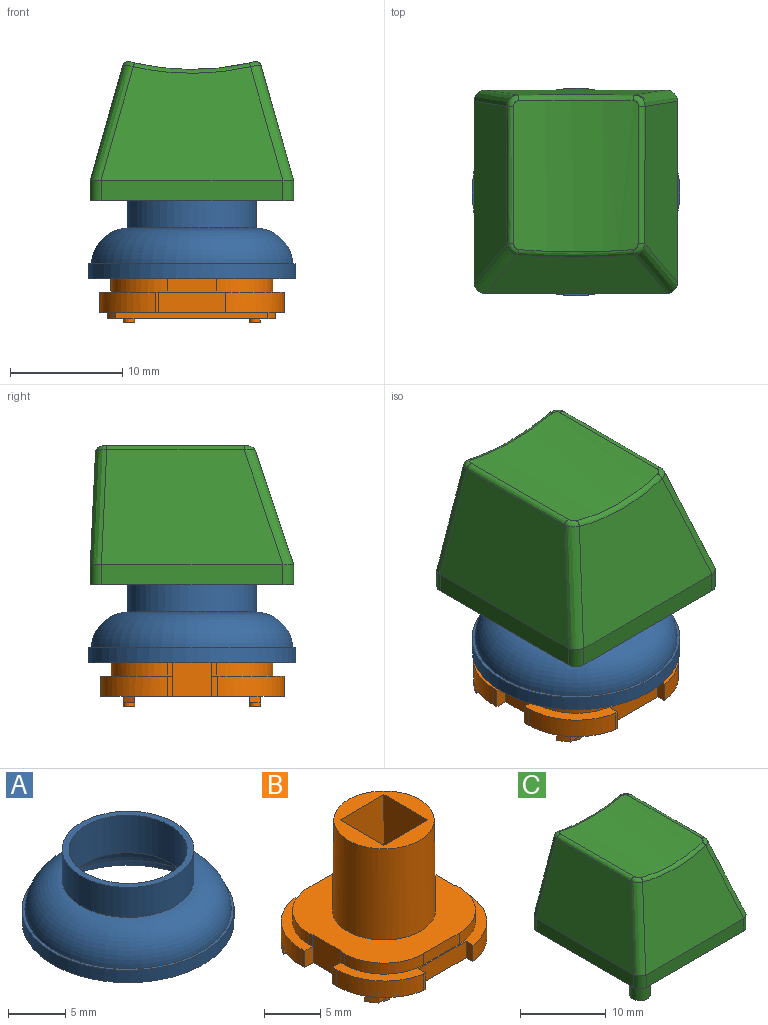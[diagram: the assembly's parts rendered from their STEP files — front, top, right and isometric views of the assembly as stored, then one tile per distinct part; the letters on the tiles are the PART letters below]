
ASSEMBLY  parts=3 mates=2
PART A: 9 faces, bbox 19.5x19.5x7.7 mm
  f0: cylinder r=9.25mm len=18.5mm, axis (0,0,1), area 76.2mm2, adj f1,f8
  f1: plane 18.5x18.5mm, normal (0,0,-1), area 41.8mm2, adj f0,f2
  f2: cylinder r=8.5mm len=17mm, axis (0,0,1), area 27.5mm2, adj f1,f3
  f3: torus R=5.16mm, axis (0,0,1), area 232.3mm2, adj f2,f4
  f4: cylinder r=5.15mm len=10.3mm, axis (0,0,1), area 129.4mm2, adj f3,f5
  f5: plane 11.5x11.5mm, normal (0,0,1), area 20.5mm2, adj f4,f6
  f6: cylinder r=5.75mm len=11.5mm, axis (0,0,1), area 115.6mm2, adj f5,f7
  f7: torus R=5.6mm, axis (0,0,1), area 243.6mm2, adj f6,f8
  f8: plane 18.5x18.5mm, normal (0,0,1), area 14.3mm2, adj f0,f7
PART B: 86 faces, bbox 16.4x16.4x13.7 mm
  f0: plane 6x1.8mm, normal (0,1,0), area 10.8mm2, adj f3,f10,f11,f12
  f1: plane 1x1mm, normal (0,0,-1), area 0.8mm2, adj f13
  f2: plane 1x1mm, normal (0,0,-1), area 0.8mm2, adj f14
  f3: plane 1.8x0.85mm, normal (1,0,0), area 1.5mm2, adj f0,f11,f12,f26
  f4: plane 1.2x0.45mm, normal (-1,0,0), area 0.5mm2, adj f5,f11,f27,f28
  f5: revolved ~5x5mm, area 9.4mm2, adj f4,f6,f11,f28
  f6: plane 4.4x1.2mm, normal (0,1,0), area 5.3mm2, adj f5,f7,f11,f28
  f7: revolved ~5x5mm, area 9.4mm2, adj f6,f9,f11,f28
  f8: revolved ~9.8x9.13mm, area 277.6mm2, adj f19,f28
  f9: plane 1.2x0.45mm, normal (1,0,0), area 0.5mm2, adj f7,f11,f28,f29
  f10: plane 1.8x0.85mm, normal (-1,0,0), area 1.5mm2, adj f0,f11,f12,f31
  f11: plane 16.4x6.4mm, normal (0,0,1), area 17.2mm2, adj f0,f3,f4,f5,f6,f7,f9,f10
  f12: plane 13.52x2.05mm, normal (0,0,-1), area 17.2mm2, adj f0,f3,f10,f15,f26,f31
  f13: revolved ~1x1mm, area 0.9mm2, adj f1,f32,f33
  f14: revolved ~1x1mm, area 0.9mm2, adj f2,f33,f34
  f15: plane 13.52x0.6mm, normal (0,1,0), area 8.1mm2, adj f12,f32,f33,f34,f35,f36
  f16: plane 2.8x0.75mm, normal (0,0,-1), area 2.1mm2, adj f40,f41,f42,f43
  f17: plane 2.8x0.75mm, normal (0,0,-1), area 2.1mm2, adj f44,f45,f46,f47
  f18: plane 2.8x0.75mm, normal (0,0,-1), area 2.1mm2, adj f48,f49,f50,f51
  f19: plane 8.9x8.9mm, normal (0,0,1), area 32mm2, adj f8,f43,f47,f51,f52
  f20: plane 2.8x0.75mm, normal (0,0,-1), area 2.1mm2, adj f37,f38,f39,f52
  f21: revolved ~5x5mm, area 9.4mm2, adj f22,f24,f28,f55
  f22: plane 4.4x1.2mm, normal (0,-1,0), area 5.3mm2, adj f21,f23,f28,f55
  f23: revolved ~5x5mm, area 9.4mm2, adj f22,f28,f53,f55
  f24: plane 1.2x0.45mm, normal (1,0,0), area 0.5mm2, adj f21,f28,f55,f57
  f25: plane 1.8x0.45mm, normal (-1,0,0), area 0.8mm2, adj f11,f26,f27,f58
  f26: revolved ~5.95x5.2mm, area 15.5mm2, adj f3,f11,f12,f25,f35,f58
  f27: plane 3x1.1mm, normal (0,-1,0), area 2.1mm2, adj f4,f11,f25,f28,f58,f59,f72
  f28: plane 14.4x14.4mm, normal (0,0,1), area 119.7mm2, adj f4,f5,f6,f7,f8,f9,f21,f22
  f29: plane 3x1.1mm, normal (0,-1,0), area 2.1mm2, adj f9,f11,f28,f30,f60,f61,f72
  f30: plane 1.8x0.45mm, normal (1,0,0), area 0.8mm2, adj f11,f29,f31,f61
  f31: revolved ~5.95x5.2mm, area 15.5mm2, adj f10,f11,f12,f30,f36,f61
  f32: plane 1.86x1mm, normal (0,0,-1), area 1.1mm2, adj f13,f15,f36,f62
  f33: plane 11.2x1mm, normal (0,0,-1), area 10.4mm2, adj f13,f14,f15,f62
  f34: plane 1.85x1mm, normal (0,0,-1), area 1.1mm2, adj f14,f15,f35,f62
  f35: revolved ~1x0.69mm, area 0.7mm2, adj f15,f26,f34,f62
  f36: revolved ~1x0.69mm, area 0.7mm2, adj f15,f31,f32,f62
  f37: plane 5.9x0.75mm, normal (0,1,0), area 4.4mm2, adj f20,f38,f52,f63
  f38: plane 5.9x2.8mm, normal (1,0,0), area 16.5mm2, adj f20,f37,f39,f63
  f39: plane 5.9x0.75mm, normal (0,-1,0), area 4.4mm2, adj f20,f38,f52,f63
  f40: plane 5.9x0.75mm, normal (1,0,0), area 4.4mm2, adj f16,f41,f43,f63
  f41: plane 5.9x2.8mm, normal (0,-1,0), area 16.5mm2, adj f16,f40,f42,f63
  f42: plane 5.9x0.75mm, normal (-1,0,0), area 4.4mm2, adj f16,f41,f43,f63
  f43: plane 12.8x5.5mm, normal (0,-1,0), area 53.9mm2, adj f16,f19,f40,f42,f47,f52,f63
  f44: plane 5.9x0.75mm, normal (0,-1,0), area 4.4mm2, adj f17,f45,f47,f63
  f45: plane 5.9x2.8mm, normal (-1,0,0), area 16.5mm2, adj f17,f44,f46,f63
  f46: plane 5.9x0.75mm, normal (0,1,0), area 4.4mm2, adj f17,f45,f47,f63
  f47: plane 12.8x5.5mm, normal (-1,0,0), area 53.9mm2, adj f17,f19,f43,f44,f46,f51,f63
  f48: plane 5.9x0.75mm, normal (-1,0,0), area 4.4mm2, adj f18,f49,f51,f63
  f49: plane 5.9x2.8mm, normal (0,1,0), area 16.5mm2, adj f18,f48,f50,f63
  f50: plane 5.9x0.75mm, normal (1,0,0), area 4.4mm2, adj f18,f49,f51,f63
  f51: plane 12.8x5.5mm, normal (0,1,0), area 53.9mm2, adj f18,f19,f47,f48,f50,f52,f63
  f52: plane 12.8x5.5mm, normal (1,0,0), area 53.9mm2, adj f19,f20,f37,f39,f43,f51,f63
  f53: plane 1.2x0.45mm, normal (-1,0,0), area 0.5mm2, adj f23,f28,f55,f64
  f54: plane 1.8x0.2mm, normal (0,-1,0), area 0.4mm2, adj f55,f66,f70,f77
  f55: plane 16.4x6.45mm, normal (0,0,1), area 17.6mm2, adj f21,f22,f23,f24,f53,f54,f56,f57
  f56: plane 1.8x0.45mm, normal (1,0,0), area 0.8mm2, adj f55,f57,f69,f71
  f57: plane 3x1.1mm, normal (0,1,0), area 2.1mm2, adj f24,f28,f55,f56,f60,f71,f72
  f58: plane 3.35x1.93mm, normal (0,0,-1), area 3.5mm2, adj f25,f26,f27,f62,f72
  f59: plane 3.5x3mm, normal (-1,0,0), area 10.5mm2, adj f27,f28,f64,f72
  f60: plane 3.5x3mm, normal (1,0,0), area 10.5mm2, adj f28,f29,f57,f72
  f61: plane 3.35x1.93mm, normal (0,0,-1), area 3.5mm2, adj f29,f30,f31,f62,f72
  f62: plane 14.91x0.6mm, normal (0,-1,0), area 8.9mm2, adj f32,f33,f34,f35,f36,f58,f61,f72
  f63: plane 9.2x9.2mm, normal (0,0,-1), area 27.8mm2, adj f37,f38,f39,f40,f41,f42,f43,f44
  f64: plane 3x1.1mm, normal (0,1,0), area 2.1mm2, adj f28,f53,f55,f59,f65,f72,f73
  f65: plane 1.8x0.53mm, normal (-1,0,0), area 1mm2, adj f55,f64,f70,f73
  f66: plane 1.8x0.9mm, normal (1,0,0), area 1.6mm2, adj f54,f55,f67,f77
  f67: plane 6x1.8mm, normal (0,-1,0), area 10.8mm2, adj f55,f66,f68,f77
  f68: plane 1.8x0.85mm, normal (-1,0,0), area 1.5mm2, adj f55,f67,f69,f77
  f69: revolved ~5.95x5.2mm, area 15.5mm2, adj f55,f56,f68,f71,f75,f77
  f70: revolved ~5.92x5mm, area 15.2mm2, adj f54,f55,f65,f73,f77,f78
  f71: plane 3.35x1.93mm, normal (0,0,-1), area 3.5mm2, adj f56,f57,f69,f72,f79
  f72: plane 14.4x10.2mm, normal (0,0,-1), area 76.3mm2, adj f27,f29,f57,f58,f59,f60,f61,f62
  f73: plane 3.35x1.93mm, normal (0,0,-1), area 3.6mm2, adj f64,f65,f70,f72,f79
  f74: plane 1x1mm, normal (0,0,-1), area 0.8mm2, adj f80
  f75: revolved ~1x0.69mm, area 0.7mm2, adj f69,f76,f79,f81
  f76: plane 1.86x1mm, normal (0,0,-1), area 1.1mm2, adj f75,f79,f80,f81
  f77: plane 13.59x2.1mm, normal (0,0,-1), area 17.5mm2, adj f54,f66,f67,f68,f69,f70,f81
  f78: revolved ~1x0.67mm, area 0.7mm2, adj f70,f79,f81,f82
  f79: plane 14.95x0.6mm, normal (0,1,0), area 9mm2, adj f71,f72,f73,f75,f76,f78,f82,f83
  f80: revolved ~1x1mm, area 0.9mm2, adj f74,f76,f83
  f81: plane 13.59x0.6mm, normal (0,-1,0), area 8.2mm2, adj f75,f76,f77,f78,f82,f83
  f82: plane 1.9x1mm, normal (0,0,-1), area 1.2mm2, adj f78,f79,f81,f84
  f83: plane 11.2x1mm, normal (0,0,-1), area 10.4mm2, adj f79,f80,f81,f84
  f84: revolved ~1x1mm, area 0.9mm2, adj f82,f83,f85
  f85: plane 1x1mm, normal (0,0,-1), area 0.8mm2, adj f84
PART C: 42 faces, bbox 22.3x23.8x26.3 mm
  f0: plane 18.1x18.1mm, normal (0,0,-1), area 67.5mm2, adj f1,f2,f3,f4,f10,f12,f14,f16
  f1: plane 16.1x1.8mm, normal (1,0,0), area 29mm2, adj f0,f8,f10,f16
  f2: plane 16.1x1.8mm, normal (0,1,0), area 29mm2, adj f0,f5,f14,f15,f16,f17
  f3: plane 16.1x1.8mm, normal (-1,0,0), area 29mm2, adj f0,f6,f12,f14
  f4: plane 16.1x1.8mm, normal (0,-1,0), area 29mm2, adj f0,f7,f10,f12
  f5: plane 16.05x10.01mm, normal (0,1,0.05), area 128.4mm2, adj f2,f15,f17,f20
  f6: bspline ~18.1x10.8mm, area 150.9mm2, adj f3,f12,f13,f14,f15,f19
  f7: plane 16.2x10.15mm, normal (0,-0.95,0.32), area 138.2mm2, adj f4,f10,f11,f12,f13,f23
  f8: bspline ~18.1x10.8mm, area 150.9mm2, adj f1,f10,f11,f16,f17,f24
  f9: cylinder r=22.9mm len=13.25mm, axis (0,-1,0), area 147.9mm2, adj f18,f19,f20,f21,f22,f23,f24,f25
  f10: cylinder r=1mm len=1.86mm, axis (0,0,-1), area 2.9mm2, adj f0,f1,f4,f7,f8,f11
  f11: bspline ~15.43x6.05mm, area 16.5mm2, adj f7,f8,f10,f25
  f12: cylinder r=1mm len=1.86mm, axis (0,0,1), area 2.9mm2, adj f0,f3,f4,f6,f7,f13
  f13: bspline ~15.43x6.05mm, area 16.5mm2, adj f6,f7,f12,f21
  f14: cylinder r=1mm len=1.81mm, axis (0,0,-1), area 2.8mm2, adj f0,f2,f3,f6,f15
  f15: bspline ~14.79x5.07mm, area 16.5mm2, adj f2,f5,f6,f14,f18
  f16: cylinder r=1mm len=1.81mm, axis (0,0,1), area 2.8mm2, adj f0,f1,f2,f8,f17
  f17: bspline ~14.79x5.07mm, area 16.5mm2, adj f2,f5,f8,f16,f22
  f18: bspline ~1.22x1.12mm, area 1mm2, adj f9,f15,f19,f20
  f19: bspline ~20.03x0.64mm, area 9.4mm2, adj f6,f9,f18,f21
  f20: bspline ~10.39x1.05mm, area 7.9mm2, adj f5,f9,f18,f22
  f21: bspline ~1.2x1.05mm, area 0.8mm2, adj f9,f13,f19,f23
  f22: bspline ~1.28x1.06mm, area 1mm2, adj f9,f17,f20,f24
  f23: bspline ~10.42x0.92mm, area 6.5mm2, adj f7,f9,f21,f25
  f24: bspline ~20.03x0.64mm, area 9.4mm2, adj f8,f9,f22,f25
  f25: bspline ~1.23x1.07mm, area 0.8mm2, adj f9,f11,f23,f24
  f26: plane 16.1x1.66mm, normal (-1,0,0), area 26.7mm2, adj f0,f27,f29,f32,f33
  f27: plane 16.1x1.78mm, normal (0,-1,0), area 28.6mm2, adj f0,f26,f28,f30,f31,f33
  f28: plane 16.1x1.66mm, normal (1,0,0), area 26.7mm2, adj f0,f27,f29,f31,f32
  f29: plane 16.1x1.64mm, normal (0,1,0), area 26.3mm2, adj f0,f26,f28,f32
  f30: plane 16.09x9.58mm, normal (0,-1,-0.05), area 122.9mm2, adj f27,f31,f33,f34
  f31: offset ~20.1x12.8mm, area 142.6mm2, adj f27,f28,f30,f32,f34
  f32: plane 16.5x10.06mm, normal (0,0.95,-0.32), area 131.7mm2, adj f26,f28,f29,f31,f33,f34
  f33: offset ~20.1x12.8mm, area 142.6mm2, adj f26,f27,f30,f32,f34
  f34: cylinder r=23.9mm len=12.41mm, axis (0,-1,0), area 104.9mm2, adj f30,f31,f32,f33,f36,f37,f38,f39
  f35: plane 5.3x5.3mm, normal (0,0,-1), area 23.6mm2, adj f36,f37,f38,f39,f40
  f36: plane 16.95x5.3mm, normal (0,1,0), area 89.3mm2, adj f34,f35,f37,f38
  f37: plane 16.95x5.3mm, normal (1,0,0), area 89.8mm2, adj f34,f35,f36,f39
  f38: plane 16.95x5.3mm, normal (-1,0,0), area 89.8mm2, adj f34,f35,f36,f39
  f39: plane 16.95x5.3mm, normal (0,-1,0), area 89.3mm2, adj f34,f35,f37,f38
  f40: cylinder r=1.2mm len=3.5mm, axis (0,0,1), area 26.4mm2, adj f35,f41
  f41: plane 2.4x2.4mm, normal (0,0,-1), area 4.5mm2, adj f40
PLACE A t=(0,0,3)mm
PLACE B at identity fixed
PLACE C t=(0,0,9.9)mm
MATE fastened B.f19 <-> C.f40  axis (0,0,1) through (0,0,12.8)mm
MATE fastened B.f28 <-> A.f0  axis (0,0,1) through (0,0,3)mm
